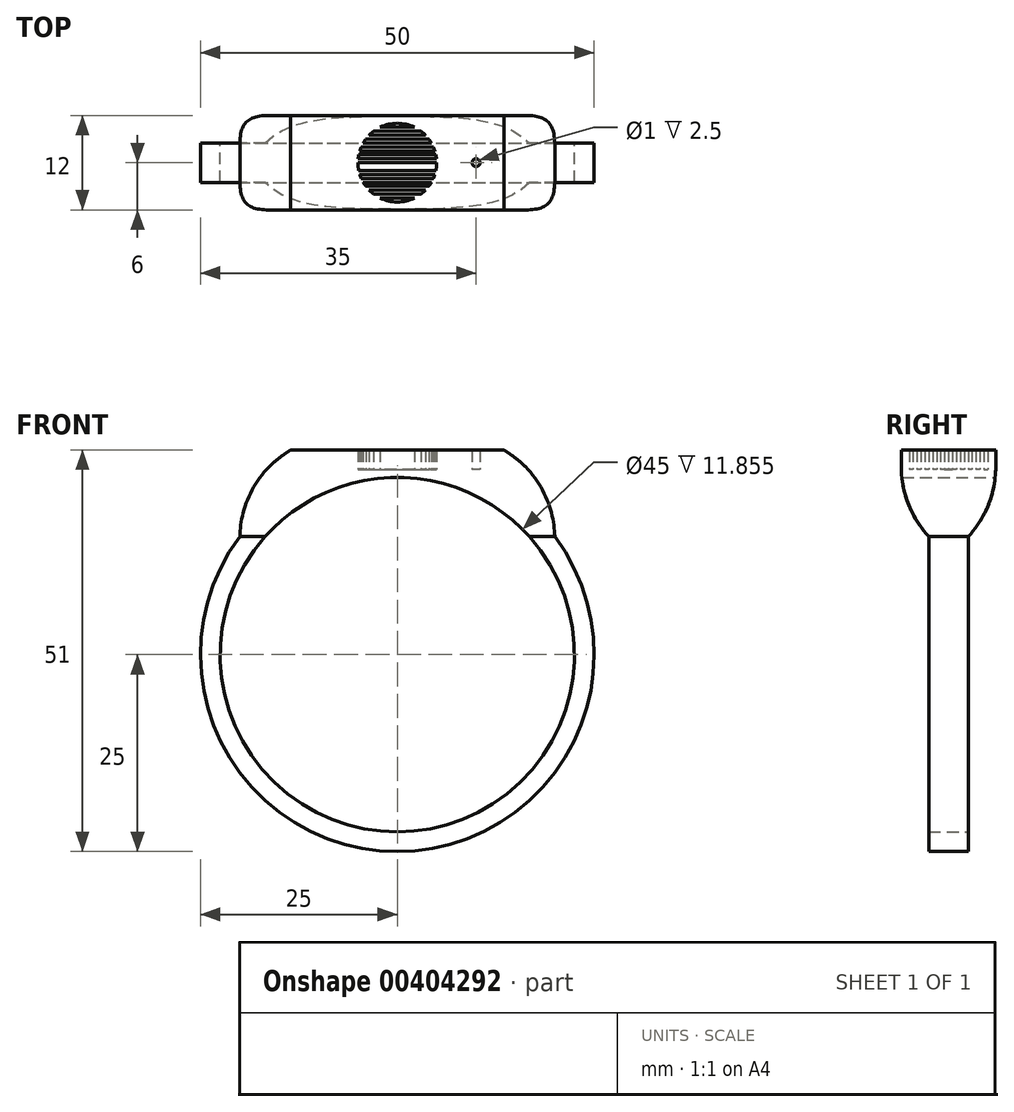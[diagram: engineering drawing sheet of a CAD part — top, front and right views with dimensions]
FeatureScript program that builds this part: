
annotation { "Feature Type Name" : "Feature", "Feature Type Description" : "" }
export const myFeature = defineFeature(function(context is Context, id is Id, definition is map)
    precondition{}
    {
        {
            var Q0;
            Q0=qCreatedBy(makeId("Front.planeOp"),FACE);
            var sketch = newSketch(context, id + "F0", { "sketchPlane" : qUnion([Q0])});
            skCircle(sketch, "E0", {"center": v(0, 0) * mm, "radius": 25 * mm});
            skCircle(sketch, "E1", {"center": v(0, 0) * mm, "radius": 22.5 * mm});
            skLineSegment(sketch, "E2", {"start": v(-20, 15) * mm, "end": v(-16.77, 15) * mm});
            skLineSegment(sketch, "E3", {"start": v(20, 15) * mm, "end": v(16.77, 15) * mm});
            skLineSegment(sketch, "E4", {"start": v(-20, 15) * mm, "end": v(-20, 20) * mm});
            skLineSegment(sketch, "E5", {"start": v(20, 15) * mm, "end": v(20, 20) * mm});
            skPoint(sketch, "E6", {"position": v(0, 22.5) * mm});
            skArc(sketch, "E7", {"start": v(20, 20) * mm, "mid": v(0, 30) * mm, "end": v(-20, 20) * mm});
            skLineSegment(sketch, "E8", {"start": v(-13.56, 26) * mm, "end": v(13.56, 26) * mm});
            skPoint(sketch, "E9", {"position": v(-13.56, 26) * mm});
            skPoint(sketch, "E10", {"position": v(13.56, 26) * mm});
            skSolve(sketch);
        }
        {
            var Q0;
            Q0=makeQuery(id+"F0.imprint","IMPRINT",FACE,{"disambiguationData":[TD([[makeQuery(id+"F0.imprint","IMPRINT",EDGE,{"derivedFrom":sQuery(id+"F0.wireOp",EDGE,"E1")}),-1.0]])]});
            extrude(context, id + "F1", {"entities" : qUnion([Q0]), "depth" : 2.5 * mm, "hasSecondDirection" : true, "secondDirectionOppositeDirection" : true, "secondDirectionDepth" : 2.5 * mm});
        }
        {
            var Q0;
            {var subQ0=sQuery(id+"F0.wireOp",EDGE,"E2");Q0=makeQuery(id+"F0.imprint","IMPRINT",FACE,{"disambiguationData":[TD([[makeQuery(id+"F0.imprint","IMPRINT",EDGE,{"derivedFrom":subQ0}),1.0]])]});}
            var Q1;
            {var subQ0=sQuery(id+"F0.wireOp",EDGE,"1f85ef3d-5dfe-47ac-9454-f6da41c13103");Q1=makeQuery(id+"F0.imprint","IMPRINT",FACE,{"disambiguationData":[TD([[makeQuery(id+"F0.imprint","IMPRINT",EDGE,{"derivedFrom":subQ0}),1.0]])]});}
            var Q2;
            {var subQ6=sQuery(id+"F0.wireOp",EDGE,"E4");Q2=makeQuery(id+"F0.imprint","IMPRINT",FACE,{"disambiguationData":[TD([[makeQuery(id+"F0.imprint","IMPRINT",EDGE,{"derivedFrom":subQ6}),-1.0]])]});}
            extrude(context, id + "F2", {"entities" : qUnion([Q0, Q1, Q2]), "operationType" : NewBodyOperationType.ADD, "depth" : 6 * mm, "hasSecondDirection" : true, "secondDirectionOppositeDirection" : true, "secondDirectionDepth" : 6 * mm});
        }
        {
            var Q0;
            Q0=makeQuery(id+"F2.opExtrude","SWEPT_EDGE",EDGE,{"disambiguationData":[OSD([sQuery(id+"F0.wireOp",EDGE,"E4"),sQuery(id+"F0.wireOp",EDGE,"E7")])]});
            var Q1;
            Q1=makeQuery(id+"F2.opExtrude","SWEPT_EDGE",EDGE,{"disambiguationData":[OSD([sQuery(id+"F0.wireOp",EDGE,"E5"),sQuery(id+"F0.wireOp",EDGE,"E7")])]});
            fillet(context, id + "F3", {"entities" : qUnion([Q0, Q1]), "radius" : 13 * mm, "tangentPropagation" : true, "allowEdgeOverflow" : false});
        }
        {
            var Q0;
            Q0=makeQuery(id+"F2.opExtrude","CAP_EDGE",EDGE,{"disambiguationData":[OSD([sQuery(id+"F0.wireOp",EDGE,"E3")])],"isStart":false});
            var Q1;
            Q1=makeQuery(id+"F2.opExtrude","CAP_EDGE",EDGE,{"disambiguationData":[OSD([sQuery(id+"F0.wireOp",EDGE,"E3")])],"isStart":true});
            fillet(context, id + "F4", {"entities" : qUnion([Q0, Q1]), "radius" : 13 * mm, "tangentPropagation" : true, "allowEdgeOverflow" : false});
        }
        {
            var Q0;
            Q0=qCreatedBy(makeId("Top.planeOp"),FACE);
            var sketch = newSketch(context, id + "F5", { "sketchPlane" : qUnion([Q0])});
            skCircle(sketch, "E11", {"center": v(0, 0) * mm, "radius": 5 * mm});
            skLineSegment(sketch, "E12", {"start": v(-5, 0) * mm, "end": v(5, 0) * mm});
            skLineSegment(sketch, "E13", {"start": v(-4.97, -0.5) * mm, "end": v(4.97, -0.5) * mm});
            skLineSegment(sketch, "E14", {"start": v(-4.9, -1) * mm, "end": v(4.9, -1) * mm});
            skLineSegment(sketch, "E15", {"start": v(-4.77, -1.5) * mm, "end": v(4.77, -1.5) * mm});
            skLineSegment(sketch, "E16", {"start": v(-4.58, -2) * mm, "end": v(4.58, -2) * mm});
            skLineSegment(sketch, "E17", {"start": v(-4.33, -2.5) * mm, "end": v(4.33, -2.5) * mm});
            skLineSegment(sketch, "E18", {"start": v(-4, -3) * mm, "end": v(4, -3) * mm});
            skLineSegment(sketch, "E19", {"start": v(-3.57, -3.5) * mm, "end": v(3.57, -3.5) * mm});
            skLineSegment(sketch, "E20", {"start": v(-3, -4) * mm, "end": v(3, -4) * mm});
            skLineSegment(sketch, "E21", {"start": v(-2.18, -4.5) * mm, "end": v(2.18, -4.5) * mm});
            skLineSegment(sketch, "E22", {"start": v(-4.97, 0.5) * mm, "end": v(4.97, 0.5) * mm});
            skLineSegment(sketch, "E23", {"start": v(-4.9, 1) * mm, "end": v(4.9, 1) * mm});
            skLineSegment(sketch, "E24", {"start": v(-4.77, 1.5) * mm, "end": v(4.77, 1.5) * mm});
            skLineSegment(sketch, "E25", {"start": v(-4.58, 2) * mm, "end": v(4.58, 2) * mm});
            skLineSegment(sketch, "E26", {"start": v(-4.33, 2.5) * mm, "end": v(4.33, 2.5) * mm});
            skLineSegment(sketch, "E27", {"start": v(-4, 3) * mm, "end": v(4, 3) * mm});
            skLineSegment(sketch, "E28", {"start": v(-3.57, 3.5) * mm, "end": v(3.57, 3.5) * mm});
            skLineSegment(sketch, "E29", {"start": v(-3, 4) * mm, "end": v(3, 4) * mm});
            skLineSegment(sketch, "E30", {"start": v(-2.18, 4.5) * mm, "end": v(2.18, 4.5) * mm});
            skLineSegment(sketch, "E31", {"start": v(0, 0) * mm, "end": v(10, 0) * mm});
            skCircle(sketch, "E32", {"center": v(10, 0) * mm, "radius": 0.5 * mm});
            skSolve(sketch);
        }
        {
            var Q0;
            Q0=makeQuery(id+"F5.imprint","IMPRINT",FACE,{"disambiguationData":[TD([[makeQuery(id+"F5.imprint","IMPRINT",EDGE,{"derivedFrom":sQuery(id+"F5.wireOp",EDGE,"E32")}),1.0]])]});
            var Q1;
            {var subQ0=sQuery(id+"F5.wireOp",EDGE,"E30");Q1=makeQuery(id+"F5.imprint","IMPRINT",FACE,{"disambiguationData":[TD([[makeQuery(id+"F5.imprint","IMPRINT",EDGE,{"derivedFrom":subQ0}),1.0]])]});}
            var Q2;
            {var subQ0=sQuery(id+"F5.wireOp",EDGE,"E21");Q2=makeQuery(id+"F5.imprint","IMPRINT",FACE,{"disambiguationData":[TD([[makeQuery(id+"F5.imprint","IMPRINT",EDGE,{"derivedFrom":subQ0}),-1.0]])]});}
            var Q3;
            {var subQ0=sQuery(id+"F5.wireOp",EDGE,"E22");Q3=makeQuery(id+"F5.imprint","IMPRINT",FACE,{"disambiguationData":[TD([[makeQuery(id+"F5.imprint","IMPRINT",EDGE,{"derivedFrom":subQ0}),1.0]])]});}
            var Q4;
            {var subQ0=sQuery(id+"F5.wireOp",EDGE,"E24");Q4=makeQuery(id+"F5.imprint","IMPRINT",FACE,{"disambiguationData":[TD([[makeQuery(id+"F5.imprint","IMPRINT",EDGE,{"derivedFrom":subQ0}),1.0]])]});}
            var Q5;
            {var subQ0=sQuery(id+"F5.wireOp",EDGE,"E26");Q5=makeQuery(id+"F5.imprint","IMPRINT",FACE,{"disambiguationData":[TD([[makeQuery(id+"F5.imprint","IMPRINT",EDGE,{"derivedFrom":subQ0}),1.0]])]});}
            var Q6;
            {var subQ0=sQuery(id+"F5.wireOp",EDGE,"E28");Q6=makeQuery(id+"F5.imprint","IMPRINT",FACE,{"disambiguationData":[TD([[makeQuery(id+"F5.imprint","IMPRINT",EDGE,{"derivedFrom":subQ0}),1.0]])]});}
            var Q7;
            {var subQ0=sQuery(id+"F5.wireOp",EDGE,"E12");Q7=makeQuery(id+"F5.imprint","IMPRINT",FACE,{"disambiguationData":[TD([[makeQuery(id+"F5.imprint","IMPRINT",EDGE,{"derivedFrom":subQ0}),-1.0]])]});}
            var Q8;
            {var subQ0=sQuery(id+"F5.wireOp",EDGE,"E13");Q8=makeQuery(id+"F5.imprint","IMPRINT",FACE,{"disambiguationData":[TD([[makeQuery(id+"F5.imprint","IMPRINT",EDGE,{"derivedFrom":subQ0}),-1.0]])]});}
            var Q9;
            {var subQ0=sQuery(id+"F5.wireOp",EDGE,"E15");Q9=makeQuery(id+"F5.imprint","IMPRINT",FACE,{"disambiguationData":[TD([[makeQuery(id+"F5.imprint","IMPRINT",EDGE,{"derivedFrom":subQ0}),-1.0]])]});}
            var Q10;
            {var subQ0=sQuery(id+"F5.wireOp",EDGE,"E17");Q10=makeQuery(id+"F5.imprint","IMPRINT",FACE,{"disambiguationData":[TD([[makeQuery(id+"F5.imprint","IMPRINT",EDGE,{"derivedFrom":subQ0}),-1.0]])]});}
            var Q11;
            {var subQ0=sQuery(id+"F5.wireOp",EDGE,"E19");Q11=makeQuery(id+"F5.imprint","IMPRINT",FACE,{"disambiguationData":[TD([[makeQuery(id+"F5.imprint","IMPRINT",EDGE,{"derivedFrom":subQ0}),-1.0]])]});}
            extrude(context, id + "F6", {"entities" : qUnion([Q0, Q1, Q2, Q3, Q4, Q5, Q6, Q7, Q8, Q9, Q10, Q11]), "operationType" : NewBodyOperationType.REMOVE, "depth" : 28.7 * mm, "hasSecondDirection" : true, "secondDirectionOppositeDirection" : false, "secondDirectionDepth" : 23.5 * mm});
        }
    });
